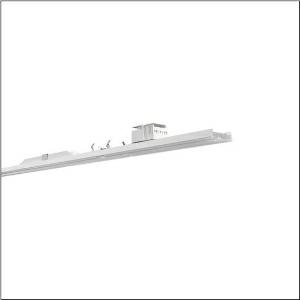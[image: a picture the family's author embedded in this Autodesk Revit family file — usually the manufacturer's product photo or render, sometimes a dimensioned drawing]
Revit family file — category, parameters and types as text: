
# Revit family: licross_r__11_recessed_mo_51tl12cn48xf_e34c
name_source: partatom
category: Lighting Fixtures
units: mm (PartAtom-declared; Revit-internal decimal feet)

## family parameters
Cut with Voids When Loaded = No
Host = Face
Light Source = No
Part Type = Normal
Room Calculation Point = No
Round Connector Dimension = Use Diameter
Shared = No

## types (1)
- --- (1 x LED, 8280 lm, 48 W, 4000K)
    Apparent Load = 48 VA
    CIE Flux Codes = 67 92 99 100 100
    Color Rendering = 80
    Color Temperature = 4000K
    Default Elevation = 1800 mm
    Description = Licross® 11 Recessed MOluminaire insert, length: 1.500mm, width: 66mm, height: 67mm, LED rated luminous flux: 8.280lm, light colour: 840, control gear: ON/OFF Multilumen, CLOi, control gear: ECG Multilumen, with plug, 3-pole, with phase selection, mains connection: 220..240V, AC, 50/60Hz, halogen-free wiring, primary optical cover: cover, of PMMA, light emission: direct distribution, protection rating (complete): IP40, insulation class (complete): insulation class I (protective earthing), certification: CE, ENEC, VDE, protection symbol: D if used in an environment without relevant dust loads with corresponding accessories, permissible ambient temperature for indoor applications: -35..+40°C, reducing of maximum allowable ambient temperature of 5°C with ceiling mounting, corresponds to IFS (International Featured Standards) requirements for safety and quality in the food industry, packaging unit: 1 piece
    Height = 58 mm
    Lamp = 1 x LED
    Lamp Light Flux = 8280 lm
    Lamp Power = 48 W
    Lamp count = 1
    Length = 1500 mm
    Luminous efficacy = 173 lm/W
    Manufacturer = Siteco
    ModVariant = No
    Model = 51TL12CN48XF
    Mounting Place = Ceiling
    Mounting Type = Pendant
    Number of Poles = 1
    OnlyDefault = Yes
    Power Factor = 1
    Product Name = Licross® 11 Recessed MO
    Product group = luminaire insert
    ProductGroupID = 902
    Protection Class = Protection class I
    Protection Degree = IP 40
    RLX_Detail_Level = 1
    RlxData = <blob elided: 19925 chars, md5=73fae0a7>
    Socket = socket
    Standby Power = 0 W
    System Light Flux = 8280 lm
    System Power = 48 W
    Type Comments = factory setting: luminous flux: 100 % | (A | C | E) | 109 mA
    Type Image = l_1266722.jpg
    URL = http://relux.com
    VarID = @adj_139055
    Voltage = 0 V
    Weight = 0.00 kg
    Width = 66 mm

## geometry (parser evidence)
native form markers: Blend x4, Sweep x9
no freeform markers — native parametric forms only
